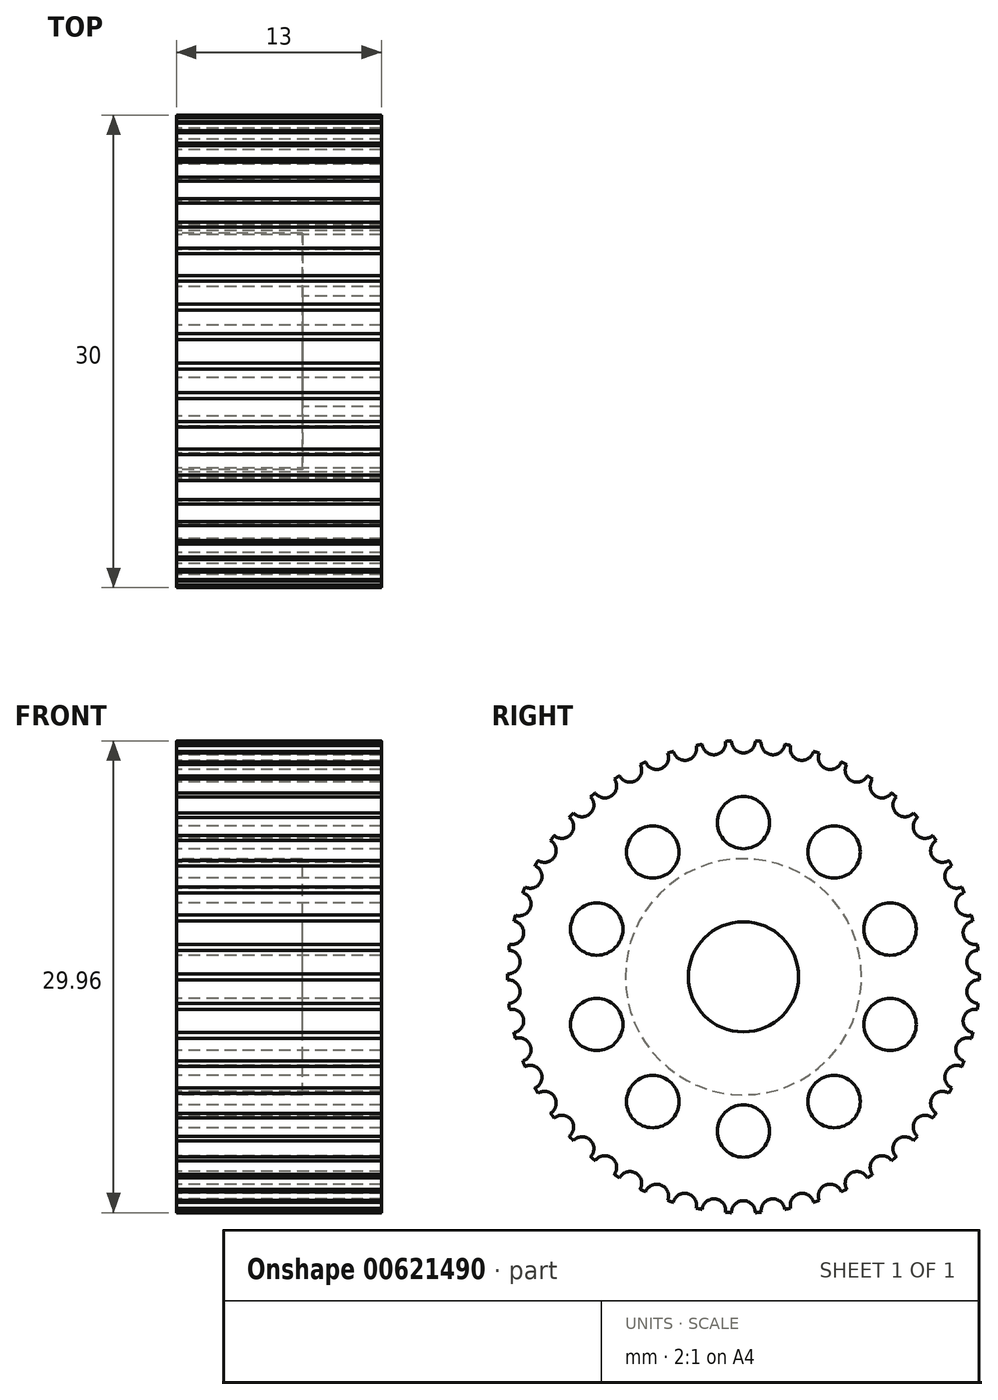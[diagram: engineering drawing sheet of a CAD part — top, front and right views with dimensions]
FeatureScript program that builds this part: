
annotation { "Feature Type Name" : "Feature", "Feature Type Description" : "" }
export const myFeature = defineFeature(function(context is Context, id is Id, definition is map)
    precondition{}
    {
        {
            var Q0;
            Q0=qCreatedBy(makeId("Right.planeOp"),FACE);
            var sketch = newSketch(context, id + "F0", { "sketchPlane" : qUnion([Q0])});
            skCircle(sketch, "E0", {"center": v(0, 0) * mm, "radius": 15 * mm});
            skCircle(sketch, "E1", {"center": v(0, 0) * mm, "radius": 7.5 * mm});
            skCircle(sketch, "E2", {"center": v(0, 0) * mm, "radius": 3.5 * mm});
            skCircle(sketch, "E3", {"center": v(0, 9.8) * mm, "radius": 1.66 * mm});
            skCircle(sketch, "E4.1.0", {"center": v(-5.76, 7.93) * mm, "radius": 1.66 * mm});
            skCircle(sketch, "E4.2.0", {"center": v(-9.32, 3.03) * mm, "radius": 1.66 * mm});
            skCircle(sketch, "E4.3.0", {"center": v(-9.32, -3.03) * mm, "radius": 1.66 * mm});
            skCircle(sketch, "E4.4.0", {"center": v(-5.76, -7.93) * mm, "radius": 1.66 * mm});
            skCircle(sketch, "E4.5.0", {"center": v(0, -9.8) * mm, "radius": 1.66 * mm});
            skCircle(sketch, "E4.6.0", {"center": v(5.76, -7.93) * mm, "radius": 1.66 * mm});
            skCircle(sketch, "E4.7.0", {"center": v(9.32, -3.03) * mm, "radius": 1.66 * mm});
            skCircle(sketch, "E4.8.0", {"center": v(9.32, 3.03) * mm, "radius": 1.66 * mm});
            skCircle(sketch, "E4.9.0", {"center": v(5.76, 7.93) * mm, "radius": 1.66 * mm});
            skSolve(sketch);
        }
        {
            var Q0;
            Q0=makeQuery(id+"F0.imprint","IMPRINT",FACE,{"disambiguationData":[TD([[makeQuery(id+"F0.imprint","IMPRINT",EDGE,{"derivedFrom":sQuery(id+"F0.wireOp",EDGE,"E1")}),-1.0]])]});
            var Q1;
            Q1=makeQuery(id+"F0.imprint","IMPRINT",FACE,{"disambiguationData":[TD([[makeQuery(id+"F0.imprint","IMPRINT",EDGE,{"derivedFrom":sQuery(id+"F0.wireOp",EDGE,"E1")}),1.0]])]});
            extrude(context, id + "F1", {"entities" : qUnion([Q0, Q1]), "depth" : 13 * mm, "offsetDistance" : 25 * mm});
        }
        {
            var Q0;
            Q0=makeQuery(id+"F0.imprint","IMPRINT",FACE,{"disambiguationData":[TD([[makeQuery(id+"F0.imprint","IMPRINT",EDGE,{"derivedFrom":sQuery(id+"F0.wireOp",EDGE,"E1")}),1.0]])]});
            extrude(context, id + "F2", {"entities" : qUnion([Q0]), "operationType" : NewBodyOperationType.REMOVE, "depth" : 8 * mm, "offsetDistance" : 25 * mm});
        }
        {
            var Q0;
            Q0=makeQuery(id+"F0.imprint","IMPRINT",FACE,{"disambiguationData":[TD([[makeQuery(id+"F0.imprint","IMPRINT",EDGE,{"derivedFrom":sQuery(id+"F0.wireOp",EDGE,"E0")}),1.0]])]});
            var sketch = newSketch(context, id + "F3", { "sketchPlane" : qUnion([Q0])});
            skCircle(sketch, "E5", {"center": v(0, 14.97) * mm, "radius": 0.75 * mm});
            skSolve(sketch);
        }
        {
            var Q0;
            {var subQ0=sQuery(id+"F3.wireOp",EDGE,"E5");var subQ1=makeQuery(id+"F0.imprint","IMPRINT",EDGE,{"derivedFrom":sQuery(id+"F0.wireOp",EDGE,"E0")});var subQ2=makeQuery(id+"F3.imprint","INTERSECT",VERTEX,{"disambiguationData":[OD(0.0)],"derivedFrom":[subQ1,subQ0]});Q0=makeQuery(id+"F3.imprint","IMPRINT",FACE,{"disambiguationData":[TD([[makeQuery(id+"F3.imprint","IMPRINT",EDGE,{"disambiguationData":[TD([[subQ2,-1.0]])],"derivedFrom":subQ0}),1.0]])]});}
            var Q1;
            {var subQ0=sQuery(id+"F3.wireOp",EDGE,"E5");var subQ1=makeQuery(id+"F0.imprint","IMPRINT",EDGE,{"derivedFrom":sQuery(id+"F0.wireOp",EDGE,"E0")});var subQ2=makeQuery(id+"F3.imprint","INTERSECT",VERTEX,{"disambiguationData":[OD(0.0)],"derivedFrom":[subQ1,subQ0]});Q1=makeQuery(id+"F3.imprint","IMPRINT",FACE,{"disambiguationData":[TD([[makeQuery(id+"F3.imprint","IMPRINT",EDGE,{"disambiguationData":[TD([[subQ2,1.0]])],"derivedFrom":subQ0}),1.0]])]});}
            extrude(context, id + "F4", {"entities" : qUnion([Q0, Q1]), "depth" : 25 * mm, "offsetDistance" : 25 * mm});
        }
        {
            var Q0;
            Q0=qCreatedBy(makeId("Top.planeOp"),FACE);
            var sketch = newSketch(context, id + "F5", { "sketchPlane" : qUnion([Q0])});
            skLineSegment(sketch, "E6", {"start": v(-19.71, 0) * mm, "end": v(30.41, 0) * mm});
            skSolve(sketch);
        }
        {
            var Q0;
            Q0=makeQuery(id+"F4.opExtrude","SWEPT_BODY",BODY,{"disambiguationData":[OSD([sQuery(id+"F3.wireOp",EDGE,"E5")])]});
            var Q1;
            Q1=sQuery(id+"F5.wireOp",EDGE,"E6");
            circularPattern(context, id + "F6", {"operationType" : NewBodyOperationType.REMOVE, "entities" : qUnion([Q0]), "axis" : qUnion([Q1]), "angle" : 360 * degree, "instanceCount" : 50, "equalSpace" : true});
        }
    });
